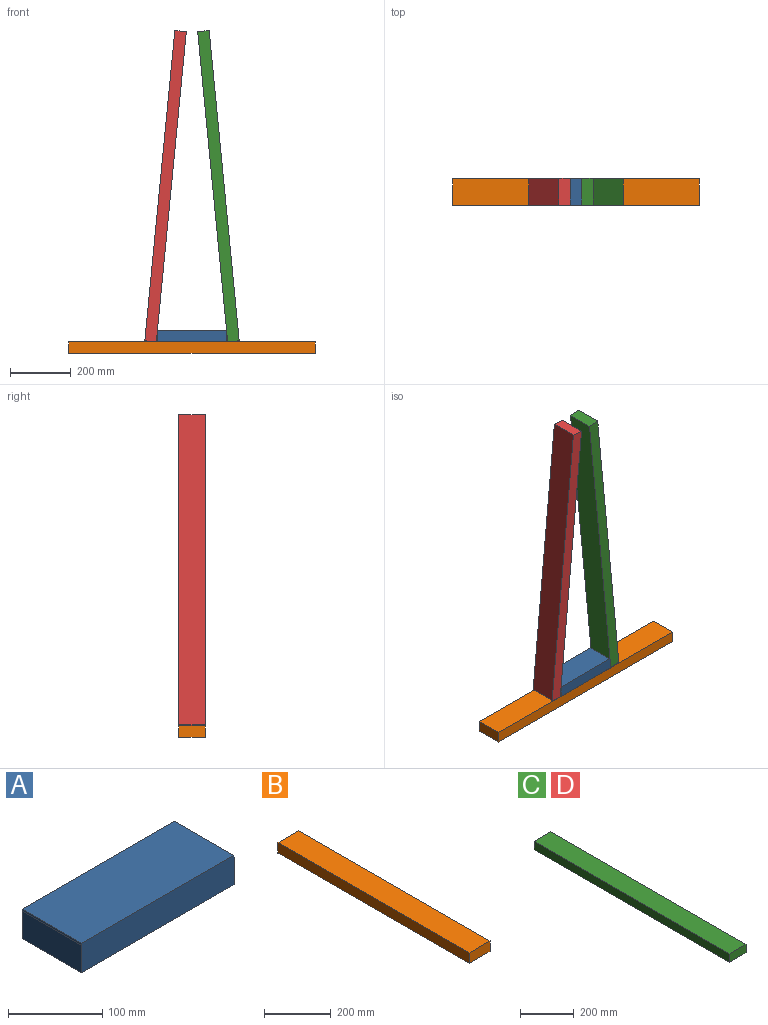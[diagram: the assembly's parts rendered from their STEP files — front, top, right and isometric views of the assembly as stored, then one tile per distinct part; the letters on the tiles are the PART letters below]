
ASSEMBLY  parts=4 mates=3
PART A: 8 faces, bbox 228.6x88.9x38.1 mm
  f0: plane 228.11x88.9mm, normal (0,0,1), area 20278.9mm2, adj f1,f4,f6,f7
  f1: plane 228.6x38.1mm, normal (0,-1,0), area 8709mm2, adj f0,f2,f3,f5,f6,f7
  f2: plane 88.9x35.56mm, normal (-1,0,0), area 3161.3mm2, adj f1,f4,f5,f6
  f3: plane 88.9x35.56mm, normal (1,0,0), area 3161.3mm2, adj f1,f4,f5,f7
  f4: plane 228.6x38.1mm, normal (0,1,0), area 8709mm2, adj f0,f2,f3,f5,f6,f7
  f5: plane 228.6x88.9mm, normal (0,0,-1), area 20322.5mm2, adj f1,f2,f3,f4
  f6: plane 88.9x2.54mm, normal (-1,0,0.1), area 226.9mm2, adj f0,f1,f2,f4
  f7: plane 88.9x2.54mm, normal (1,0,0.1), area 226.9mm2, adj f0,f1,f3,f4
PART B: 6 faces, bbox 88.9x812.8x38.1 mm
  f0: plane 812.8x88.9mm, normal (0,0,-1), area 72257.9mm2, adj f1,f3,f4,f5
  f1: plane 812.8x38.1mm, normal (1,0,0), area 30967.7mm2, adj f0,f2,f4,f5
  f2: plane 812.8x88.9mm, normal (0,0,1), area 72257.9mm2, adj f1,f3,f4,f5
  f3: plane 812.8x38.1mm, normal (-1,0,0), area 30967.7mm2, adj f0,f2,f4,f5
  f4: plane 88.9x38.1mm, normal (0,1,0), area 3387.1mm2, adj f0,f1,f2,f3
  f5: plane 88.9x38.1mm, normal (0,-1,0), area 3387.1mm2, adj f0,f1,f2,f3
PART C: 6 faces, bbox 88.9x1028.7x38.1 mm
  f0: plane 1028.7x88.9mm, normal (0,0,-1), area 91451.4mm2, adj f1,f3,f4,f5
  f1: plane 1028.7x38.1mm, normal (1,0,0), area 39193.5mm2, adj f0,f2,f4,f5
  f2: plane 1028.7x88.9mm, normal (0,0,1), area 91451.4mm2, adj f1,f3,f4,f5
  f3: plane 1028.7x38.1mm, normal (-1,0,0), area 39193.5mm2, adj f0,f2,f4,f5
  f4: plane 88.9x38.1mm, normal (0,1,0), area 3387.1mm2, adj f0,f1,f2,f3
  f5: plane 88.9x38.1mm, normal (0,-1,0), area 3387.1mm2, adj f0,f1,f2,f3
PART D: same geometry as C
PLACE A t=(114.3,44.45,0)mm
PLACE B rot(axis=(0,0,1),90deg) t=(406.4,44.45,-38.1)mm
PLACE C rot(axis=(0.6,-0.6,-0.54),123.2deg) t=(155.65,-44.45,3.83)mm
PLACE D rot(axis=(0.6,0.6,0.54),123.2deg) t=(-155.65,44.45,3.83)mm
MATE fastened C.f2 <-> A.f7  axis (-1,0,-0.1) through (117.72,0,0.17)mm
MATE fastened D.f2 <-> A.f6  axis (1,0,-0.1) through (-117.72,0,0.17)mm
MATE fastened A.f5 <-> B.f2  axis (0,0,-1) through (0,0,0)mm
